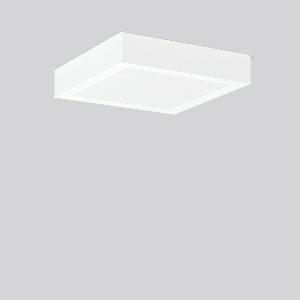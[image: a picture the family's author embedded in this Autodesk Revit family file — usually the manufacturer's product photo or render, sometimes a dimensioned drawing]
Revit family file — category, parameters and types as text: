
# Revit family: toledo_flat_square_a_672277_002_1_f107
name_source: partatom
category: Lighting Fixtures
units: mm (PartAtom-declared; Revit-internal decimal feet)

## family parameters
Cut with Voids When Loaded = No
Host = Face
Light Source = No
Part Type = Normal
Room Calculation Point = No
Round Connector Dimension = Use Diameter
Shared = No

## types (1)
- TOLEDO FLAT square A (1 x LED Modul 840, 2200 lm, 4000)
    Apparent Load = 25 VA
    CIE Flux Codes = 49 80 96 100 100
    Color Rendering = 80
    Color Temperature = 4000
    Default Elevation = 1800 mm
    Description = Series: TOLEDO FLAT square
Ultra thin surface mounted downlight. For escape route illumination. Surface mounted housing: sheet steel, powder-coated. Square cover plate: die-cast aluminium, powder coated. Light guide and diffuser made of non-yellowing PMMA, opal matt. Betriebsgeräte integriert. Einzelbatteriesystem mit automatischem Selbsttest. 
Colour: white
Length: 300 mm
Width: 300 mm
Height: 58 mm
Weight: 3.95 kg
Operating mode: maintained power mode
Duration time: 3 h
Lamp: LED
Socket: without socket
Colour temperature: 4000K
Colour rendering index (CRI): 80
System power: 25 W
Rated luminous flux: 2200 lm
Luminous flux, emergency: 430 lm
System power, emergency: -
Control gear: Regulated power supply
Protection class: I
Type of protection: IP 40
    Height = 58 mm
    Lamp = 1 x LED Modul 840
    Lamp Light Flux = 2200 lm
    Lamp count = 1
    Length = 300 mm
    Lifetime = 50000 h
    Luminous efficacy = 88 lm/W
    Manufacturer = RZB
    ModVariant = No
    Model = 672277.002.1
    Mounting Place = Ceiling
    Mounting Type = Surface mounted
    Number of Poles = 1
    OnlyDefault = Yes
    Power Factor = 1
    Product Name = TOLEDO FLAT square A
    Product group = Surface mounted downlights
    ProductGroupID = 302
    Protection Class = Protection class I
    Protection Degree = IP 40
    RLX_Detail_Level = 1
    RLX_Emergency_Light_Flux = 430 lm
    RLX_Emergency_Type = 3
    RLX_Emergency_Type_DB = Yes
    RlxData = <blob elided: 13937 chars, md5=50a4830b>
    Socket = socket
    Standby Power = 0 W
    System Light Flux = 2200 lm
    System Power = 25 W
    Type Comments = Product without accessories
    Type Image = 901554.002.jpg
    URL = http://relux.com
    VarID = ---
    Voltage = 0 V
    Weight = 0.00 kg
    Width = 300 mm

## geometry (parser evidence)
native form markers: Sweep x14
no freeform markers — native parametric forms only
